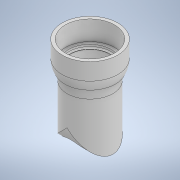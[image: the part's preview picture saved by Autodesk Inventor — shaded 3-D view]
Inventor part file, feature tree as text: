
AUTODESK INVENTOR PART (.ipt)
format: ipt  version: 2021 (Build 250183000, 183)  size: 189,952 bytes
history: native  units: mm
features: sketch x7, extrude x6, fillet x3, other x1
ambient origin geometry x8: Origin, YZ Plane, XZ Plane, XY Plane, X Axis, Y Axis, Z Axis, Center Point
bodies: Body1 (feature_tree), Body2 (feature_tree)
feature tree (17):
  other  "Sólido1"
  extrude  "Extrusión1"  Depth=70.0mm
  extrude  "Extrusión2"  Depth=35.0mm TaperAngle=0.0deg
  extrude  "Extrusión3"  Depth=35.0mm TaperAngle=0.0deg
  sketch  "Boceto4"  dims[d19=85.0mm d20=65.0mm]
  extrude  "Extrusión4"  Depth=65.0mm
  extrude  "Extrusión5"  Depth=30.0mm
  fillet  "Empalme1"  Radius=2.0mm
  fillet  "Empalme2"  Radius=30.0mm
  fillet  "Empalme3"  Radius=75.0mm
  extrude  "Extrusión6"  [1 undecoded]
  sketch  "Boceto1"  dims[d0=60.0mm d1=70.0mm]
  sketch  "Boceto2"  dims[d2=100.0mm d3=0.0mm d13=35.0mm d14=0.0mm]
  sketch  "Boceto3"  dims[d15=100.0mm d16=0.0mm d17=35.0mm d18=0.0mm]
  sketch  "Boceto5"  dims[d21=35.0mm d22=0.0mm d23=30.0mm d24=2.0mm d25=30.0mm d26=75.0mm]
  sketch  "Boceto6"  dims[d27=30.0mm d28=0.0mm]
  sketch  "Boceto7"
note: 1 required parameter value undecoded (feature->parameter linkage not recoverable at this tier; creation-order binding heuristic only, values carry confidence <= 0.55)
